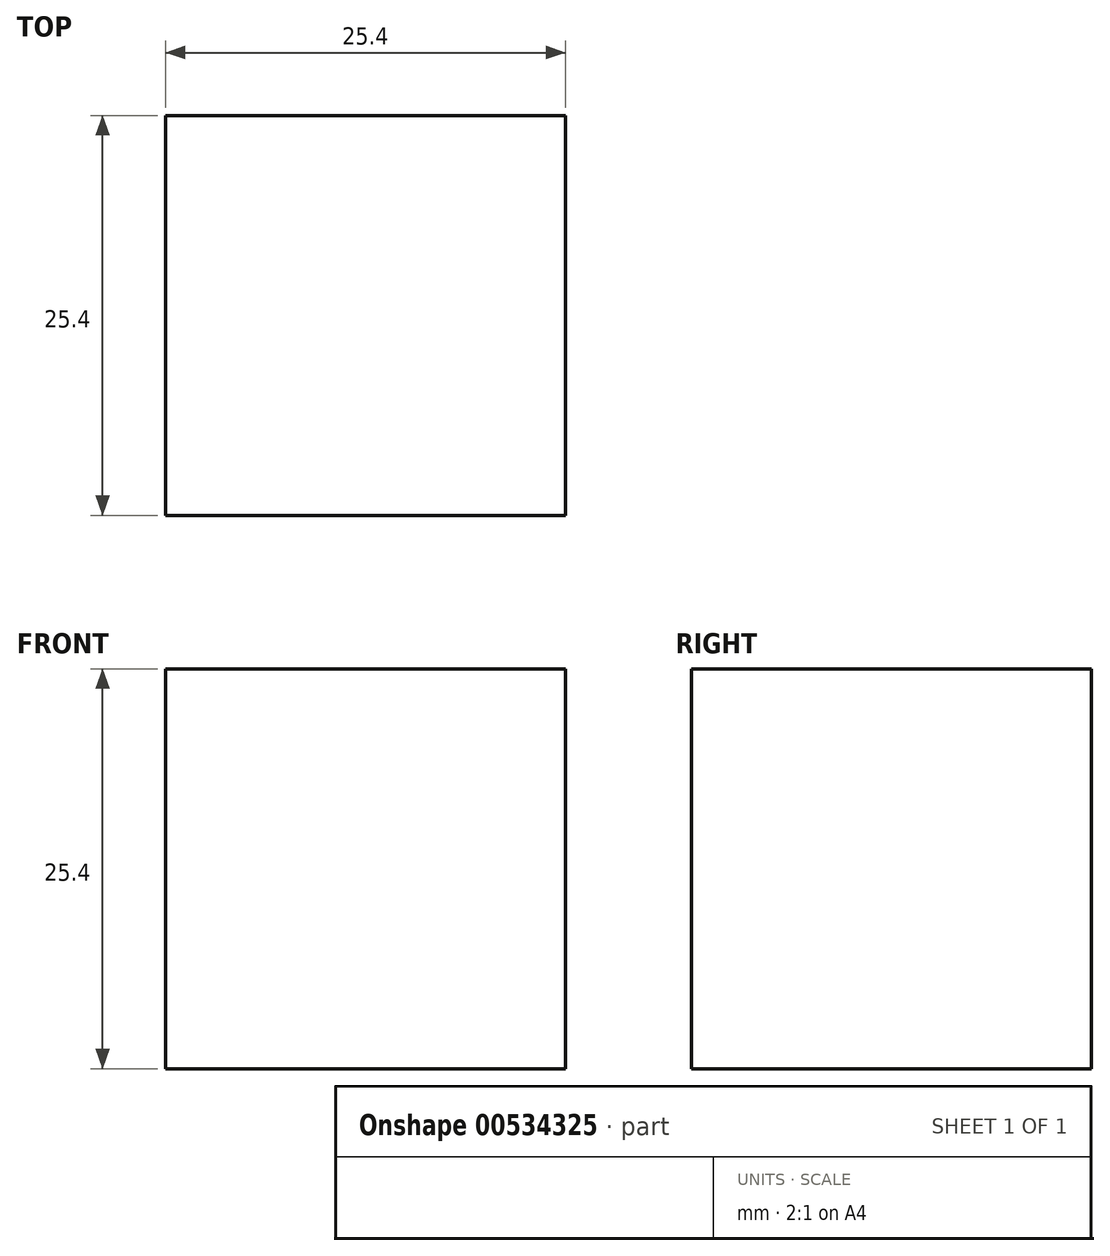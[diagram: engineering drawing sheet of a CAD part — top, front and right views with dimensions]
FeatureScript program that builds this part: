
annotation { "Feature Type Name" : "Feature", "Feature Type Description" : "" }
export const myFeature = defineFeature(function(context is Context, id is Id, definition is map)
    precondition{}
    {
        {
            var Q0;
            Q0=qCreatedBy(makeId("Front.planeOp"),FACE);
            var sketch = newSketch(context, id + "F0", { "sketchPlane" : qUnion([Q0])});
            skLineSegment(sketch, "E0.bottom", {"start": v(-58.05, 43.43) * mm, "end": v(-32.65, 43.43) * mm});
            skLineSegment(sketch, "E0.top", {"start": v(-58.05, 18.03) * mm, "end": v(-32.65, 18.03) * mm});
            skLineSegment(sketch, "E0.left", {"start": v(-58.05, 43.43) * mm, "end": v(-58.05, 18.03) * mm});
            skLineSegment(sketch, "E0.right", {"start": v(-32.65, 43.43) * mm, "end": v(-32.65, 18.03) * mm});
            skSolve(sketch);
        }
        {
            var Q0;
            Q0 = qSketchRegion(id + "F0", true);
            extrude(context, id + "F1", {"entities" : qUnion([Q0]), "depth" : 25.4 * mm, "offsetDistance" : 25.4 * mm});
        }
    });
